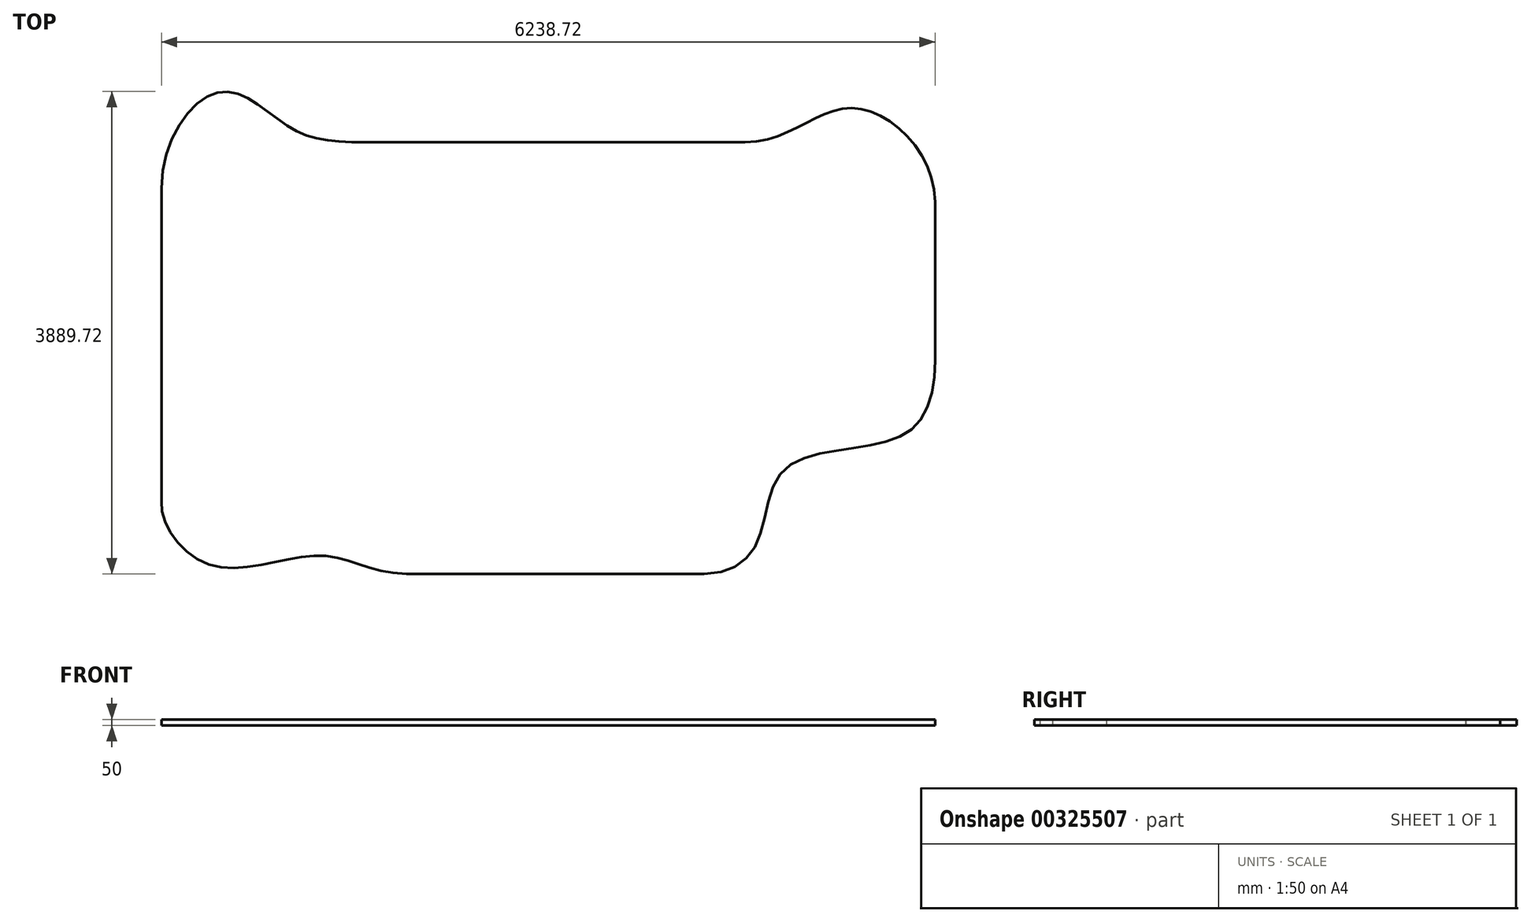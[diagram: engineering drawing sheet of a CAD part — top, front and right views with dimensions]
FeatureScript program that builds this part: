
annotation { "Feature Type Name" : "Feature", "Feature Type Description" : "" }
export const myFeature = defineFeature(function(context is Context, id is Id, definition is map)
    precondition{}
    {
        {
            var Q0;
            Q0=qCreatedBy(makeId("Top.planeOp"),FACE);
            var sketch = newSketch(context, id + "F0", { "sketchPlane" : qUnion([Q0])});
            skLineSegment(sketch, "E0.bottom", {"start": v(3125, -1950) * mm, "end": v(-3125, -1950) * mm, "construction": true});
            skLineSegment(sketch, "E0.top", {"start": v(3125, 1950) * mm, "end": v(-3120, 1950) * mm, "construction": true});
            skLineSegment(sketch, "E0.left", {"start": v(3125, -1950) * mm, "end": v(3125, 1950) * mm, "construction": true});
            skLineSegment(sketch, "E0.right", {"start": v(-3125, -1950) * mm, "end": v(-3125, 1945) * mm, "construction": true});
            skPoint(sketch, "E0.middle", {"position": v(0, 0) * mm});
            skPoint(sketch, "E1.visualSharp", {"position": v(-3125, 1950) * mm});
            skArc(sketch, "E1.filletArc", {"start": v(-3120, 1950) * mm, "mid": v(-3123.54, 1948.54) * mm, "end": v(-3125, 1945) * mm, "construction": true});
            skLineSegment(sketch, "E2", {"start": v(1258.22, -1950) * mm, "end": v(-1144.46, -1950) * mm});
            skFitSpline(sketch, "E3", {"points": [v(-1144.46, -1950) * mm, v(-1838.87, -1804.07) * mm, v(-2724.9, -1878.77) * mm, v(-3117.87, -1366) * mm], "startDerivative": vector(-2576.26, 0) * mm, "endDerivative": vector(167.48, 1754.26) * mm});
            skLineSegment(sketch, "E4", {"start": v(-3117.87, -1366) * mm, "end": v(-3117.87, 1161.56) * mm});
            skFitSpline(sketch, "E5", {"points": [v(-3117.87, 1161.56) * mm, v(-2629.69, 1938.47) * mm, v(-2068.17, 1642.4) * mm, v(-1353.52, 1530.1) * mm], "startDerivative": vector(0, 3276.29) * mm, "endDerivative": vector(2943.7, 0) * mm});
            skLineSegment(sketch, "E6", {"start": v(-1353.52, 1530.1) * mm, "end": v(1588.27, 1530.1) * mm});
            skFitSpline(sketch, "E7", {"points": [v(1588.27, 1530.1) * mm, v(2466.28, 1805.75) * mm, v(3119.68, 1050.25) * mm], "startDerivative": vector(2193.13, 0) * mm, "endDerivative": vector(0, -2308.74) * mm});
            skLineSegment(sketch, "E8", {"start": v(3119.68, 1050.25) * mm, "end": v(3119.68, -231.87) * mm});
            skFitSpline(sketch, "E9", {"points": [v(1258.22, -1950) * mm, v(1682.96, -1699.82) * mm, v(1875.64, -1140.07) * mm, v(2444.46, -938.18) * mm, v(2966.54, -752.55) * mm, v(3119.68, -231.87) * mm], "startDerivative": vector(3366.75, 0) * mm, "endDerivative": vector(0, 3016.1) * mm});
            skSolve(sketch);
        }
        {
            var Q0;
            Q0 = qConstructionFilter(qBodyType(qCreatedBy(id + "F0" ,EDGE), BodyType.WIRE), ConstructionObject.NO);
            extrude(context, id + "F1", {"bodyType" : ToolBodyType.SURFACE, "surfaceEntities" : qUnion([Q0]), "depth" : 50 * mm});
        }
    });
